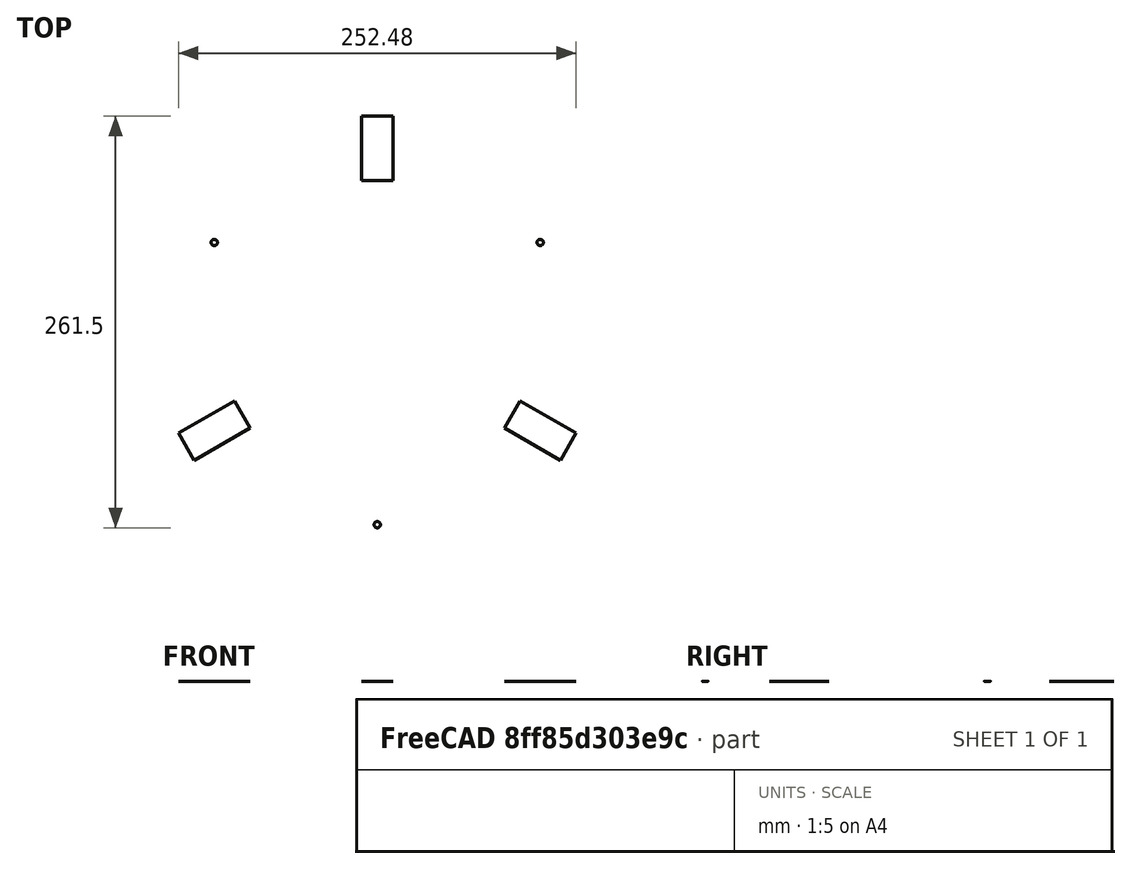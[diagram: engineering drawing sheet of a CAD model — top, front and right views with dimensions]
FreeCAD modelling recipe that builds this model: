
FCSTD DOCUMENT  (FreeCAD 0.16RUnknown)
Label: model-cylinder
License: All rights reserved
LicenseURL: http://en.wikipedia.org/wiki/All_rights_reserved
objects: Part::Part2DObjectPython×4, Part::FeaturePython×2, Spreadsheet::Sheet×1
note: 6 computed .brp shape members not serialized (recipe doc carries the construction recipe); baked Part::Feature solids carry a one-line shape summary decoded from their .brp

FEATURE [Part::Part2DObjectPython] Circle  label="circleExternal"  # Draft 2D object (typed FeaturePython)
  FirstAngle = 0
  LastAngle = 360
  MakeFace = true
  Radius = 150
  expr: Radius = prefs.circleExternal / 2
FEATURE [Part::Part2DObjectPython] Circle001  label="circleInternal"  # Draft 2D object (typed FeaturePython)
  FirstAngle = 0
  LastAngle = 360
  MakeFace = true
  Radius = 89
  expr: Radius = prefs.circleInternal / 2
FEATURE [Part::Part2DObjectPython] Rectangle  label="servo"  # Draft 2D object (typed FeaturePython)
  ChamferSize = 0
  Columns = 1
  FilletRadius = 0
  Height = 41
  Length = 20
  MakeFace = true
  Placement = pos=(-10,99,0) rot=(0,0,1;0rad)
  Rows = 1
  expr: Placement.Base.y = (prefs.circleExternal + prefs.circleInternal - 2 * prefs.servoLength) / 4
  expr: Height = prefs.servoLength
  expr: Placement.Base.x = -prefs.servoWidth / 2
FEATURE [Part::FeaturePython] Array  label="servoArray"  # Draft array (typed FeaturePython)
  Angle = 360
  ArrayType = 1
  Axis = (0,0,1)
  Base = -> Rectangle
  Center = (0,0,0)
  Fuse = false
  IntervalAxis = (0,0,0)
  IntervalX = (1,0,0)
  IntervalY = (0,1,0)
  IntervalZ = (0,0,0)
  NumberPolar = 3
  NumberX = 1
  NumberY = 1
  NumberZ = 1
  expr: NumberPolar = prefs.servoNumber
FEATURE [Part::Part2DObjectPython] Circle002  label="screw"  # Draft 2D object (typed FeaturePython)
  FirstAngle = 0
  LastAngle = 0
  MakeFace = true
  Placement = pos=(0,119.5,0) rot=(0,0,1;0rad)
  Radius = 2
  expr: Radius = prefs.screwDiameter / 2
  expr: Placement.Base.x = 0
  expr: Placement.Base.y = (prefs.circleExternal + prefs.circleInternal) / 4
FEATURE [Part::FeaturePython] Array001  label="screwArray"  # Draft array (typed FeaturePython)
  Angle = 360
  ArrayType = 1
  Axis = (0,0,1)
  Base = -> Circle002
  Center = (0,0,0)
  Fuse = false
  IntervalAxis = (0,0,0)
  IntervalX = (1,0,0)
  IntervalY = (0,1,0)
  IntervalZ = (0,0,0)
  NumberPolar = 3
  NumberX = 2
  NumberY = 2
  NumberZ = 1
  Placement = pos=(0,0,0) rot=(0,0,1;1.0472rad)
  expr: Placement.Rotation.Angle = 180 / prefs.servoNumber
  expr: NumberPolar = prefs.servoNumber
FEATURE [Spreadsheet::Sheet] Spreadsheet  label="prefs"
  cells = A2=External circle diameter; B2(circleExternal)=300; C2=mm; A3=Internal circle diameter; B3(circleInternal)=178; C3=mm; A4=Number servo; B4(servoNumber)=3; C4=mm; A5=Diameter screw; B5(screwDiameter)=4; C5=mm; A6=Width servo; B6(servoWidth)=20; C6=mm; A7=Length servo; B7(servoLength)=41; C7=mm
